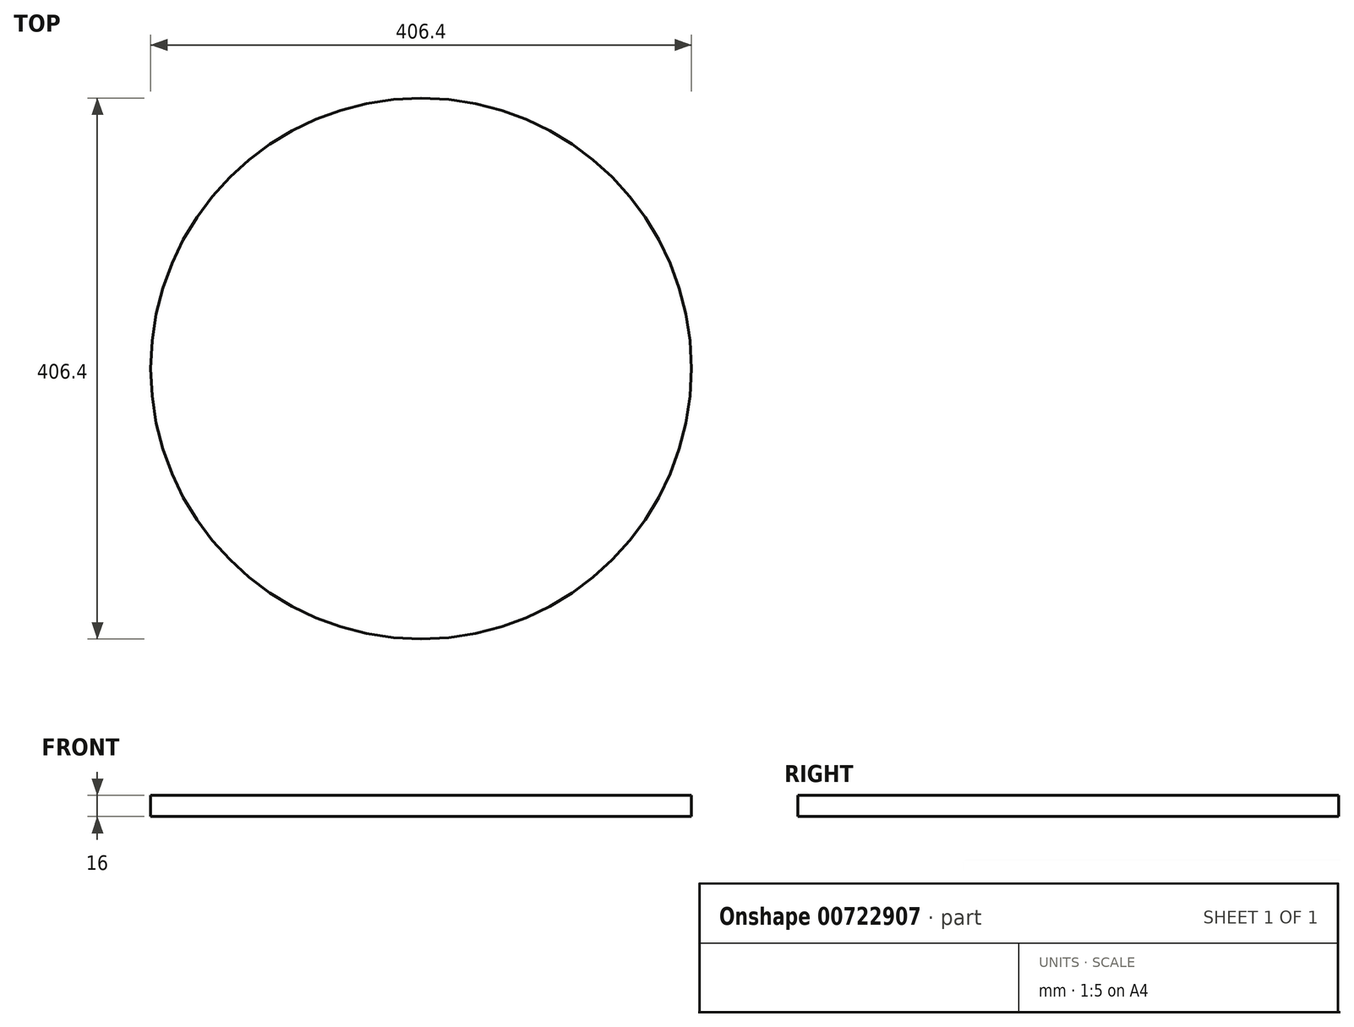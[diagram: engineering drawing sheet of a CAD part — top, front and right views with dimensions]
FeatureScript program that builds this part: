
annotation { "Feature Type Name" : "Feature", "Feature Type Description" : "" }
export const myFeature = defineFeature(function(context is Context, id is Id, definition is map)
    precondition{}
    {
        {
            var Q0;
            Q0=qCreatedBy(makeId("Top.planeOp"),FACE);
            var sketch = newSketch(context, id + "F0", { "sketchPlane" : qUnion([Q0])});
            skCircle(sketch, "E0", {"center": v(0, 0) * mm, "radius": 203.2 * mm});
            skSolve(sketch);
        }
        {
            var Q0;
            Q0=makeQuery(id+"F0.imprint","IMPRINT",FACE,{"disambiguationData":[TD([[makeQuery(id+"F0.imprint","IMPRINT",EDGE,{"derivedFrom":sQuery(id+"F0.wireOp",EDGE,"E0")}),1.0]])]});
            extrude(context, id + "F1", {"entities" : qUnion([Q0]), "depth" : 16 * mm, "offsetDistance" : 25 * mm});
        }
    });
